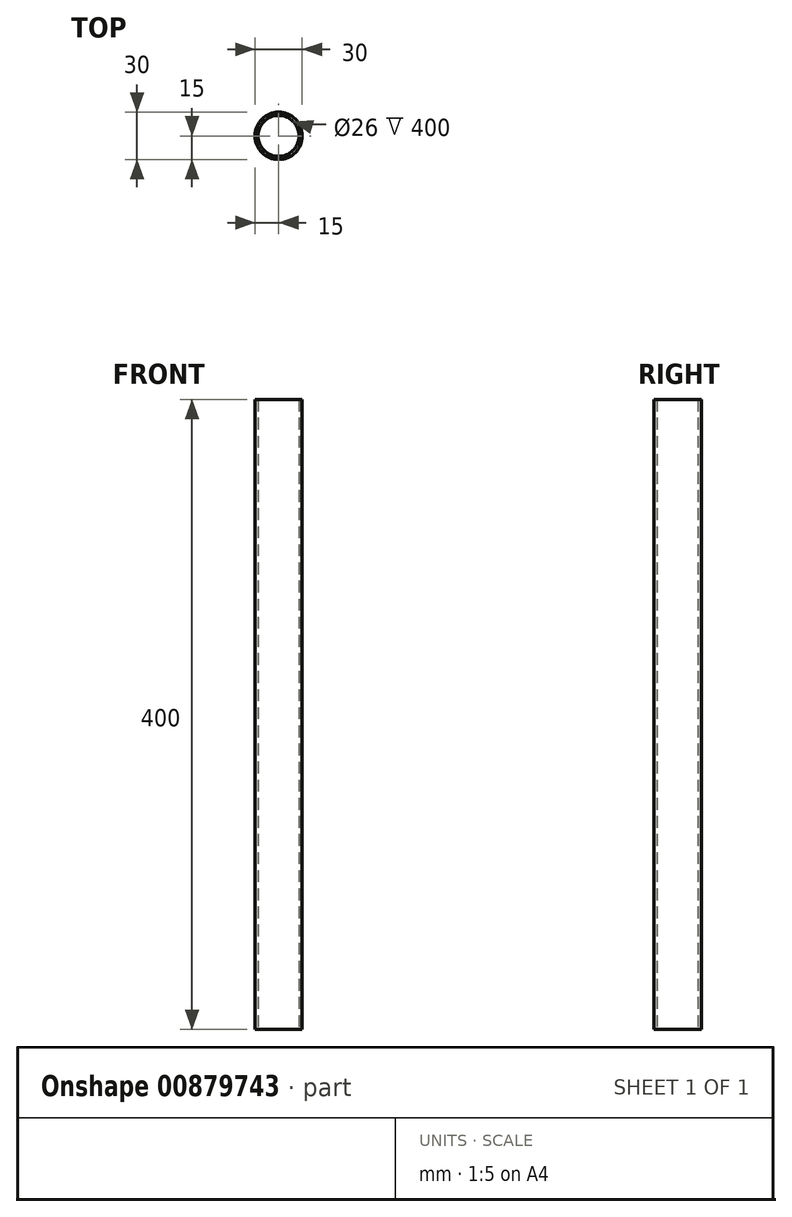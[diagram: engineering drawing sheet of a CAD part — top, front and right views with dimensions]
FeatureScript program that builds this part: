
annotation { "Feature Type Name" : "Feature", "Feature Type Description" : "" }
export const myFeature = defineFeature(function(context is Context, id is Id, definition is map)
    precondition{}
    {
        {
            var Q0;
            Q0=qCreatedBy(makeId("Top.planeOp"),FACE);
            var sketch = newSketch(context, id + "F0", { "sketchPlane" : qUnion([Q0])});
            skCircle(sketch, "E0", {"center": v(0, 0) * mm, "radius": 15 * mm});
            skCircle(sketch, "E1.0", {"center": v(0, 0) * mm, "radius": 13 * mm});
            skSolve(sketch);
        }
        {
            var Q0;
            Q0 = qSketchRegion(id + "F0", true);
            extrude(context, id + "F1", {"entities" : qUnion([Q0]), "depth" : 400 * mm, "offsetDistance" : 25 * mm});
        }
    });
